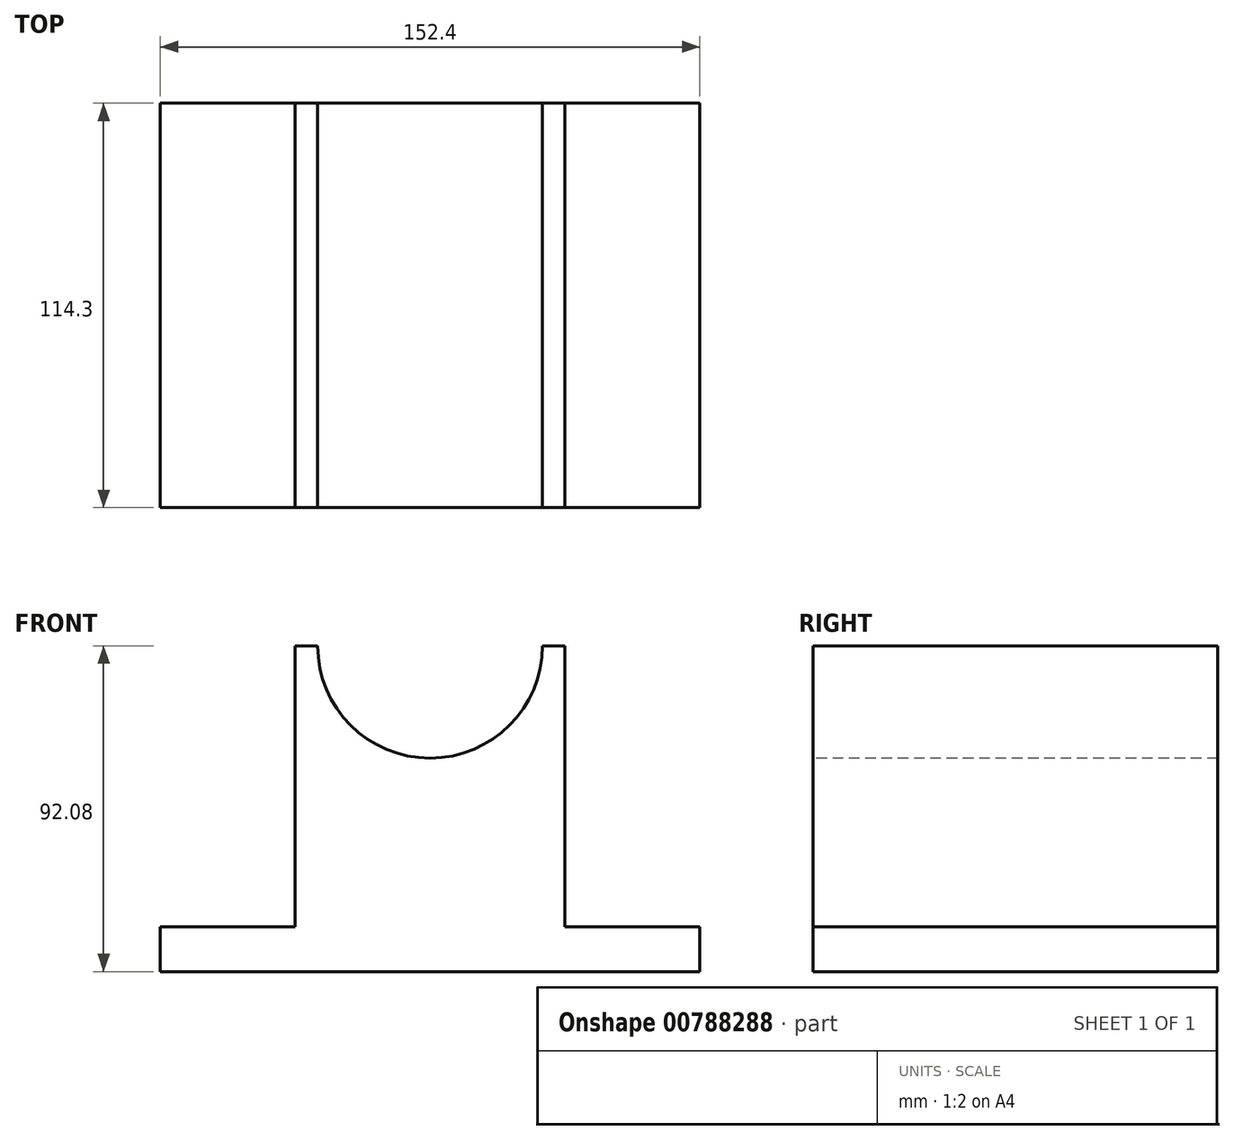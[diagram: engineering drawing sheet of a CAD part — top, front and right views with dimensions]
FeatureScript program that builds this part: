
annotation { "Feature Type Name" : "Feature", "Feature Type Description" : "" }
export const myFeature = defineFeature(function(context is Context, id is Id, definition is map)
    precondition{}
    {
        {
            var Q0;
            Q0=qCreatedBy(makeId("Front.planeOp"),FACE);
            var sketch = newSketch(context, id + "F0", { "sketchPlane" : qUnion([Q0])});
            skLineSegment(sketch, "E0", {"start": v(0, 0) * mm, "end": v(152.4, 0) * mm});
            skLineSegment(sketch, "E1", {"start": v(152.4, 0) * mm, "end": v(152.4, 12.7) * mm});
            skLineSegment(sketch, "E2", {"start": v(152.4, 12.7) * mm, "end": v(114.3, 12.7) * mm});
            skLineSegment(sketch, "E3", {"start": v(114.3, 12.7) * mm, "end": v(114.3, 92.07) * mm});
            skLineSegment(sketch, "E4", {"start": v(114.3, 92.07) * mm, "end": v(38.1, 92.07) * mm});
            skLineSegment(sketch, "E5", {"start": v(38.1, 92.07) * mm, "end": v(38.1, 12.7) * mm});
            skLineSegment(sketch, "E6", {"start": v(38.1, 12.7) * mm, "end": v(0, 12.7) * mm});
            skLineSegment(sketch, "E7", {"start": v(0, 12.7) * mm, "end": v(0, 0) * mm});
            skSolve(sketch);
        }
        {
            var Q0;
            Q0 = qSketchRegion(id + "F0", true);
            extrude(context, id + "F1", {"entities" : qUnion([Q0]), "depth" : 114.3 * mm, "offsetDistance" : 25.4 * mm});
        }
        {
            var Q0;
            Q0=makeQuery(id+"F1.opExtrude","CAP_FACE",FACE,{"disambiguationData":[OSD([sQuery(id+"F0.wireOp",EDGE,"E0"),sQuery(id+"F0.wireOp",EDGE,"E1"),sQuery(id+"F0.wireOp",EDGE,"E2"),sQuery(id+"F0.wireOp",EDGE,"E3"),sQuery(id+"F0.wireOp",EDGE,"E4"),sQuery(id+"F0.wireOp",EDGE,"E5"),sQuery(id+"F0.wireOp",EDGE,"E6"),sQuery(id+"F0.wireOp",EDGE,"E7")])],"isStart":false});
            var sketch = newSketch(context, id + "F2", { "sketchPlane" : qUnion([Q0])});
            skLineSegment(sketch, "E8", {"start": v(38.1, 92.07) * mm, "end": v(44.45, 92.07) * mm, "construction": true});
            skLineSegment(sketch, "E9", {"start": v(114.3, 92.07) * mm, "end": v(107.95, 92.07) * mm, "construction": true});
            skArc(sketch, "E10", {"start": v(44.45, 92.07) * mm, "mid": v(76.2, 60.32) * mm, "end": v(107.95, 92.07) * mm});
            skSolve(sketch);
        }
        {
            var Q0;
            Q0 = qSketchRegion(id + "F2", true);
            var Q1;
            {var subQ0=sQuery(id+"F2.wireOp",EDGE,"E10");Q1=makeQuery(id+"F2.imprint","IMPRINT",FACE,{"disambiguationData":[TD([[makeQuery(id+"F2.imprint","IMPRINT",EDGE,{"derivedFrom":subQ0}),1.0]])]});}
            extrude(context, id + "F3", {"entities" : qUnion([Q0, Q1]), "operationType" : NewBodyOperationType.REMOVE, "endBound" : BoundingType.UP_TO_NEXT, "oppositeDirection" : true, "depth" : 25.4 * mm, "offsetDistance" : 25.4 * mm});
        }
    });
